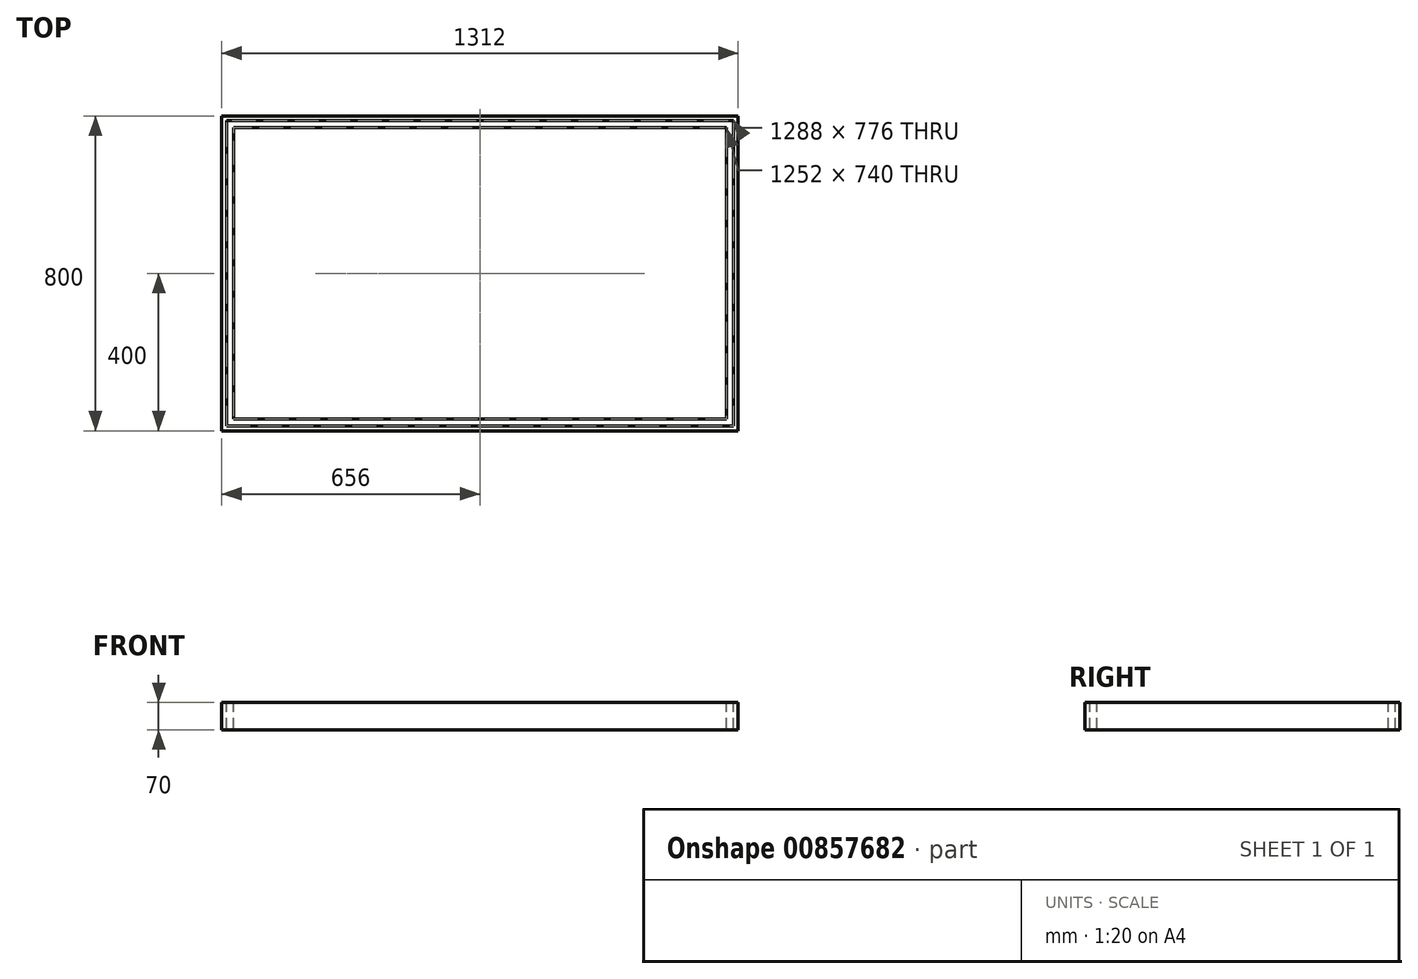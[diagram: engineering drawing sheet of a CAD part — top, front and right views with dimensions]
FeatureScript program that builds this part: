
annotation { "Feature Type Name" : "Feature", "Feature Type Description" : "" }
export const myFeature = defineFeature(function(context is Context, id is Id, definition is map)
    precondition{}
    {
        {
            var Q0;
            Q0=qCreatedBy(makeId("Top.planeOp"),FACE);
            var sketch = newSketch(context, id + "F0", { "sketchPlane" : qUnion([Q0])});
            skLineSegment(sketch, "E0.bottom", {"start": v(656, -400) * mm, "end": v(-656, -400) * mm});
            skLineSegment(sketch, "E0.top", {"start": v(656, 400) * mm, "end": v(-656, 400) * mm});
            skLineSegment(sketch, "E0.left", {"start": v(656, -400) * mm, "end": v(656, 400) * mm});
            skLineSegment(sketch, "E0.right", {"start": v(-656, -400) * mm, "end": v(-656, 400) * mm});
            skPoint(sketch, "E0.middle", {"position": v(0, 0) * mm});
            skLineSegment(sketch, "E1.0", {"start": v(644, 388) * mm, "end": v(-644, 388) * mm});
            skLineSegment(sketch, "E1.1", {"start": v(644, -388) * mm, "end": v(644, 388) * mm});
            skLineSegment(sketch, "E1.2", {"start": v(644, -388) * mm, "end": v(-644, -388) * mm});
            skLineSegment(sketch, "E1.3", {"start": v(-644, -388) * mm, "end": v(-644, 388) * mm});
            skLineSegment(sketch, "E2.0", {"start": v(626, 370) * mm, "end": v(-626, 370) * mm});
            skLineSegment(sketch, "E2.1", {"start": v(626, -388) * mm, "end": v(626, 388) * mm});
            skLineSegment(sketch, "E2.2", {"start": v(626, -370) * mm, "end": v(-626, -370) * mm});
            skLineSegment(sketch, "E2.3", {"start": v(-626, -370) * mm, "end": v(-626, 370) * mm});
            skLineSegment(sketch, "E3", {"start": v(-626, 370) * mm, "end": v(-626, 388) * mm});
            skLineSegment(sketch, "E4", {"start": v(-626, -370) * mm, "end": v(-626, -388) * mm});
            skLineSegment(sketch, "E5", {"start": v(-644, 388) * mm, "end": v(-656, 388) * mm});
            skLineSegment(sketch, "E6", {"start": v(644, 388) * mm, "end": v(656, 388) * mm});
            skLineSegment(sketch, "E7", {"start": v(644, -388) * mm, "end": v(656, -388) * mm});
            skLineSegment(sketch, "E8", {"start": v(-644, -388) * mm, "end": v(-656, -388) * mm});
            skSolve(sketch);
        }
        {
            var Q0;
            {var subQ4=sQuery(id+"F0.wireOp",EDGE,"E2.0");Q0=makeQuery(id+"F0.imprint","IMPRINT",FACE,{"disambiguationData":[TD([[makeQuery(id+"F0.imprint","IMPRINT",EDGE,{"derivedFrom":subQ4}),-1.0]])]});}
            var Q1;
            {var subQ4=sQuery(id+"F0.wireOp",EDGE,"E2.2");Q1=makeQuery(id+"F0.imprint","IMPRINT",FACE,{"disambiguationData":[TD([[makeQuery(id+"F0.imprint","IMPRINT",EDGE,{"derivedFrom":subQ4}),1.0]])]});}
            var Q2;
            {var subQ0=sQuery(id+"F0.wireOp",EDGE,"E1.3");Q2=makeQuery(id+"F0.imprint","IMPRINT",FACE,{"disambiguationData":[TD([[makeQuery(id+"F0.imprint","IMPRINT",EDGE,{"derivedFrom":subQ0}),-1.0]])]});}
            var Q3;
            {var subQ4=sQuery(id+"F0.wireOp",EDGE,"E1.1");Q3=makeQuery(id+"F0.imprint","IMPRINT",FACE,{"disambiguationData":[TD([[makeQuery(id+"F0.imprint","IMPRINT",EDGE,{"derivedFrom":subQ4}),1.0]])]});}
            extrude(context, id + "F1", {"entities" : qUnion([Q0, Q1, Q2, Q3]), "oppositeDirection" : true, "depth" : 70 * mm, "offsetDistance" : 25 * mm});
        }
        {
            var Q0;
            {var subQ4=sQuery(id+"F0.wireOp",EDGE,"E0.top");Q0=makeQuery(id+"F0.imprint","IMPRINT",FACE,{"disambiguationData":[TD([[makeQuery(id+"F0.imprint","IMPRINT",EDGE,{"derivedFrom":subQ4}),1.0]])]});}
            var Q1;
            Q1=makeQuery(id+"F0.imprint","IMPRINT",FACE,{"disambiguationData":[TD([[makeQuery(id+"F0.imprint","IMPRINT",EDGE,{"derivedFrom":sQuery(id+"F0.wireOp",EDGE,"E1.3")}),1.0]])]});
            var Q2;
            {var subQ4=sQuery(id+"F0.wireOp",EDGE,"E0.bottom");Q2=makeQuery(id+"F0.imprint","IMPRINT",FACE,{"disambiguationData":[TD([[makeQuery(id+"F0.imprint","IMPRINT",EDGE,{"derivedFrom":subQ4}),-1.0]])]});}
            var Q3;
            Q3=makeQuery(id+"F0.imprint","IMPRINT",FACE,{"disambiguationData":[TD([[makeQuery(id+"F0.imprint","IMPRINT",EDGE,{"derivedFrom":sQuery(id+"F0.wireOp",EDGE,"E1.1")}),-1.0]])]});
            extrude(context, id + "F2", {"entities" : qUnion([Q0, Q1, Q2, Q3]), "oppositeDirection" : true, "depth" : 70 * mm, "offsetDistance" : 25 * mm});
        }
    });
